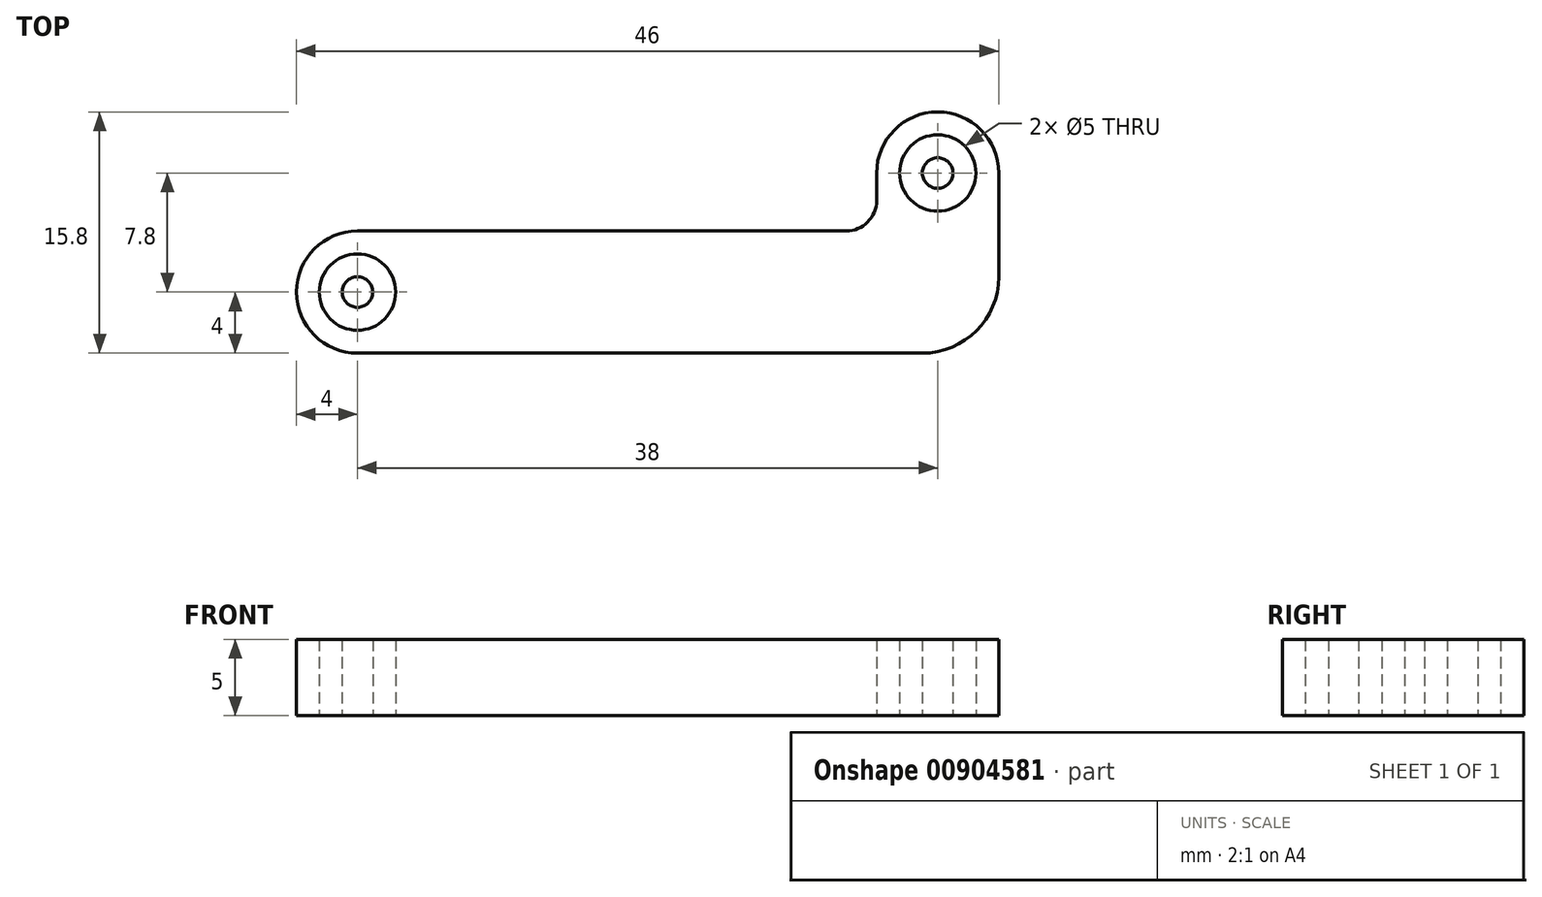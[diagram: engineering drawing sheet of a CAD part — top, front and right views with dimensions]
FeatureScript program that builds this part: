
annotation { "Feature Type Name" : "Feature", "Feature Type Description" : "" }
export const myFeature = defineFeature(function(context is Context, id is Id, definition is map)
    precondition{}
    {
        {
            var Q0;
            Q0=qCreatedBy(makeId("Top.planeOp"),FACE);
            var sketch = newSketch(context, id + "F0", { "sketchPlane" : qUnion([Q0])});
            skArc(sketch, "E0", {"start": v(0, 4) * mm, "mid": v(-4, 0) * mm, "end": v(0, -4) * mm});
            skArc(sketch, "E1", {"start": v(42, 7.8) * mm, "mid": v(38, 11.8) * mm, "end": v(34, 7.8) * mm});
            skLineSegment(sketch, "E2", {"start": v(0, 4) * mm, "end": v(32, 4) * mm});
            skLineSegment(sketch, "E3", {"start": v(34, 7.8) * mm, "end": v(34, 6) * mm});
            skLineSegment(sketch, "E4", {"start": v(42, 7.8) * mm, "end": v(42, 1) * mm});
            skLineSegment(sketch, "E5", {"start": v(0, -4) * mm, "end": v(37, -4) * mm});
            skCircle(sketch, "E6", {"center": v(0, 0) * mm, "radius": 2.5 * mm});
            skCircle(sketch, "E7", {"center": v(0, 0) * mm, "radius": 1 * mm});
            skCircle(sketch, "E8", {"center": v(38, 7.8) * mm, "radius": 2.5 * mm});
            skCircle(sketch, "E9", {"center": v(38, 7.8) * mm, "radius": 1 * mm});
            skArc(sketch, "E10", {"start": v(37, -4) * mm, "mid": v(40.54, -2.54) * mm, "end": v(42, 1) * mm});
            skArc(sketch, "E11", {"start": v(32, 4) * mm, "mid": v(33.41, 4.59) * mm, "end": v(34, 6) * mm});
            skSolve(sketch);
        }
        {
            var Q0;
            Q0=makeQuery(id+"F0.imprint","IMPRINT",FACE,{"disambiguationData":[TD([[makeQuery(id+"F0.imprint","IMPRINT",EDGE,{"derivedFrom":sQuery(id+"F0.wireOp",EDGE,"E0")}),1.0]])]});
            var Q1;
            Q1=makeQuery(id+"F0.imprint","IMPRINT",FACE,{"disambiguationData":[TD([[makeQuery(id+"F0.imprint","IMPRINT",EDGE,{"derivedFrom":sQuery(id+"F0.wireOp",EDGE,"E9")}),1.0]])]});
            var Q2;
            Q2=makeQuery(id+"F0.imprint","IMPRINT",FACE,{"disambiguationData":[TD([[makeQuery(id+"F0.imprint","IMPRINT",EDGE,{"derivedFrom":sQuery(id+"F0.wireOp",EDGE,"E7")}),1.0]])]});
            extrude(context, id + "F1", {"entities" : qUnion([Q0, Q1, Q2]), "endBound" : BoundingType.SYMMETRIC, "depth" : 5 * mm, "offsetDistance" : 25.4 * mm});
        }
    });
